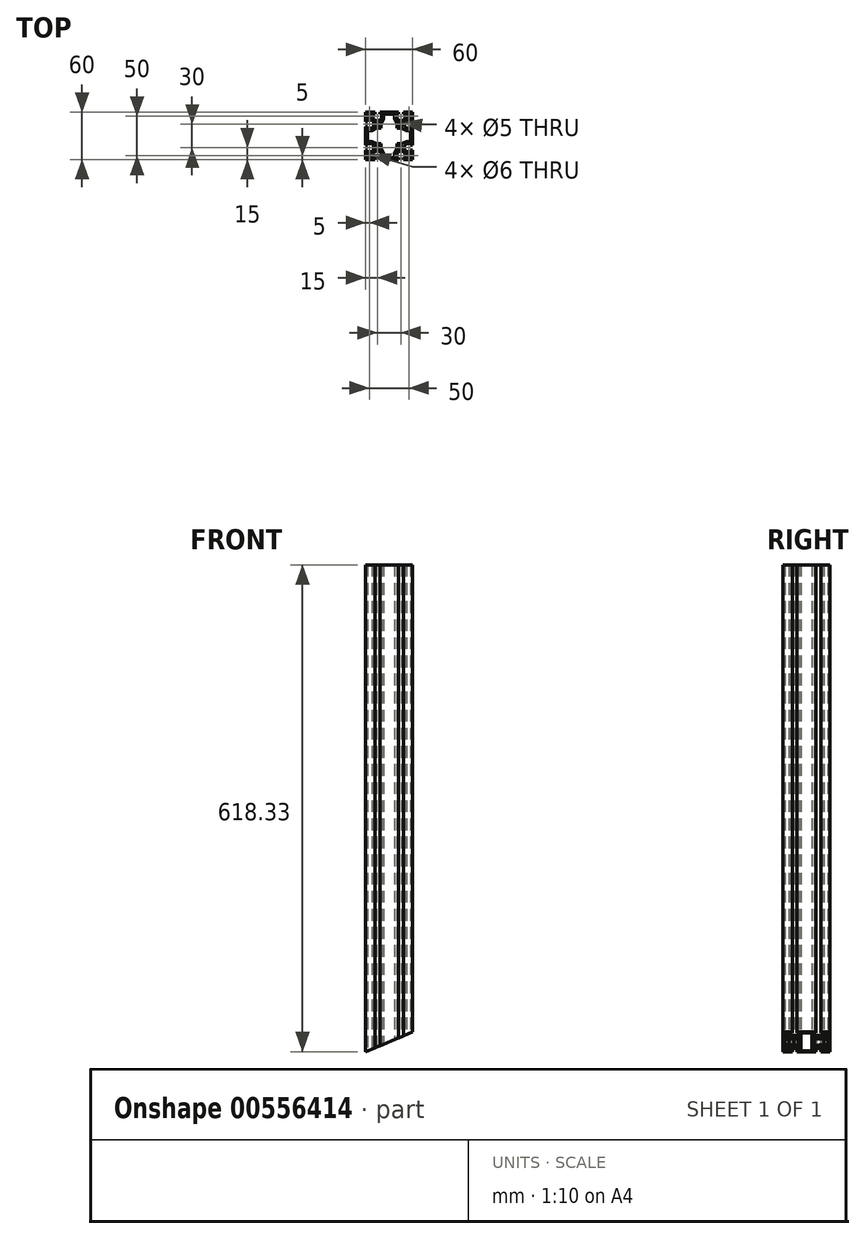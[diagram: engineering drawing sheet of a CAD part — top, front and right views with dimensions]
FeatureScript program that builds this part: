
annotation { "Feature Type Name" : "Feature", "Feature Type Description" : "" }
export const myFeature = defineFeature(function(context is Context, id is Id, definition is map)
    precondition{}
    {
        {
            var Q0;
            Q0=qCreatedBy(makeId("Top.planeOp"),FACE);
            var sketch = newSketch(context, id + "F0", { "sketchPlane" : qUnion([Q0])});
            skLineSegment(sketch, "E0.bottom", {"start": v(30, -30) * mm, "end": v(-30, -30) * mm});
            skLineSegment(sketch, "E0.top", {"start": v(30, 30) * mm, "end": v(-30, 30) * mm});
            skLineSegment(sketch, "E0.left", {"start": v(30, -30) * mm, "end": v(30, 30) * mm});
            skLineSegment(sketch, "E0.right", {"start": v(-30, -30) * mm, "end": v(-30, 30) * mm});
            skPoint(sketch, "E0.middle", {"position": v(0, 0) * mm});
            skLineSegment(sketch, "E1.top", {"start": v(-11.85, 30) * mm, "end": v(-18.15, 30) * mm});
            skLineSegment(sketch, "E1.left", {"start": v(-11.85, 27.5) * mm, "end": v(-11.85, 30) * mm});
            skLineSegment(sketch, "E1.right", {"start": v(-18.15, 27.5) * mm, "end": v(-18.15, 30) * mm});
            skPoint(sketch, "E1.middle", {"position": v(-15, 28.75) * mm});
            skLineSegment(sketch, "E2.bottom", {"start": v(-9.85, 27.5) * mm, "end": v(-11.85, 27.5) * mm});
            skLineSegment(sketch, "E2.left", {"start": v(-9.85, 27.5) * mm, "end": v(-9.85, 21.55) * mm});
            skLineSegment(sketch, "E2.right", {"start": v(-20.15, 27.5) * mm, "end": v(-20.15, 21.55) * mm});
            skPoint(sketch, "E2.middle", {"position": v(-15, 24.52) * mm});
            skArc(sketch, "E3", {"start": v(-20.15, 21.55) * mm, "mid": v(-15, 19.5) * mm, "end": v(-9.85, 21.55) * mm});
            skPoint(sketch, "E4.MirrorP", {"position": v(15, 24.52) * mm});
            skPoint(sketch, "E5.MirrorP", {"position": v(15, 28.75) * mm});
            skLineSegment(sketch, "E6.MirrorCS", {"start": v(11.85, 27.5) * mm, "end": v(11.85, 30) * mm});
            skLineSegment(sketch, "E7.MirrorCS", {"start": v(18.15, 27.5) * mm, "end": v(18.15, 30) * mm});
            skLineSegment(sketch, "E8.MirrorCS", {"start": v(9.85, 27.5) * mm, "end": v(11.85, 27.5) * mm});
            skLineSegment(sketch, "E9.MirrorCS", {"start": v(9.85, 27.5) * mm, "end": v(9.85, 21.55) * mm});
            skArc(sketch, "E10.MirrorCS", {"start": v(20.15, 21.55) * mm, "mid": v(15, 19.5) * mm, "end": v(9.85, 21.55) * mm});
            skLineSegment(sketch, "E11.MirrorCS", {"start": v(20.15, 27.5) * mm, "end": v(20.15, 21.55) * mm});
            skLineSegment(sketch, "E12.MirrorCS", {"start": v(11.85, 30) * mm, "end": v(18.15, 30) * mm});
            skLineSegment(sketch, "E13.1.0", {"start": v(27.5, 20.15) * mm, "end": v(21.55, 20.15) * mm});
            skLineSegment(sketch, "E13.1.1", {"start": v(27.5, 9.85) * mm, "end": v(21.55, 9.85) * mm});
            skArc(sketch, "E13.1.2", {"start": v(21.55, 20.15) * mm, "mid": v(19.5, 15) * mm, "end": v(21.55, 9.85) * mm});
            skLineSegment(sketch, "E13.1.3", {"start": v(27.5, -9.85) * mm, "end": v(21.55, -9.85) * mm});
            skLineSegment(sketch, "E13.1.4", {"start": v(27.5, -20.15) * mm, "end": v(21.55, -20.15) * mm});
            skPoint(sketch, "E13.1.5", {"position": v(28.75, 15) * mm});
            skPoint(sketch, "E13.1.6", {"position": v(28.75, -15) * mm});
            skArc(sketch, "E13.1.7", {"start": v(21.55, -20.15) * mm, "mid": v(19.5, -15) * mm, "end": v(21.55, -9.85) * mm});
            skPoint(sketch, "E13.1.8", {"position": v(24.52, -15) * mm});
            skPoint(sketch, "E13.1.9", {"position": v(24.52, 15) * mm});
            skLineSegment(sketch, "E13.1.10", {"start": v(27.5, 9.85) * mm, "end": v(27.5, 20.15) * mm});
            skLineSegment(sketch, "E13.1.11", {"start": v(27.5, -11.85) * mm, "end": v(27.5, -18.15) * mm});
            skLineSegment(sketch, "E13.1.12", {"start": v(30, 11.85) * mm, "end": v(30, 18.15) * mm});
            skLineSegment(sketch, "E13.1.13", {"start": v(30, -11.85) * mm, "end": v(30, -18.15) * mm});
            skLineSegment(sketch, "E13.1.14", {"start": v(27.5, 18.15) * mm, "end": v(30, 18.15) * mm});
            skLineSegment(sketch, "E13.1.15", {"start": v(27.5, 11.85) * mm, "end": v(30, 11.85) * mm});
            skLineSegment(sketch, "E13.1.16", {"start": v(27.5, 11.85) * mm, "end": v(27.5, 18.15) * mm});
            skLineSegment(sketch, "E13.1.17", {"start": v(27.5, -9.85) * mm, "end": v(27.5, -20.15) * mm});
            skLineSegment(sketch, "E13.1.18", {"start": v(27.5, -18.15) * mm, "end": v(30, -18.15) * mm});
            skLineSegment(sketch, "E13.1.19", {"start": v(27.5, -11.85) * mm, "end": v(30, -11.85) * mm});
            skLineSegment(sketch, "E13.2.0", {"start": v(20.15, -27.5) * mm, "end": v(20.15, -21.55) * mm});
            skLineSegment(sketch, "E13.2.1", {"start": v(9.85, -27.5) * mm, "end": v(9.85, -21.55) * mm});
            skArc(sketch, "E13.2.2", {"start": v(20.15, -21.55) * mm, "mid": v(15, -19.5) * mm, "end": v(9.85, -21.55) * mm});
            skLineSegment(sketch, "E13.2.3", {"start": v(-9.85, -27.5) * mm, "end": v(-9.85, -21.55) * mm});
            skLineSegment(sketch, "E13.2.4", {"start": v(-20.15, -27.5) * mm, "end": v(-20.15, -21.55) * mm});
            skPoint(sketch, "E13.2.5", {"position": v(15, -28.75) * mm});
            skPoint(sketch, "E13.2.6", {"position": v(-15, -28.75) * mm});
            skArc(sketch, "E13.2.7", {"start": v(-20.15, -21.55) * mm, "mid": v(-15, -19.5) * mm, "end": v(-9.85, -21.55) * mm});
            skPoint(sketch, "E13.2.8", {"position": v(-15, -24.52) * mm});
            skPoint(sketch, "E13.2.9", {"position": v(15, -24.52) * mm});
            skLineSegment(sketch, "E13.2.10", {"start": v(9.85, -27.5) * mm, "end": v(20.15, -27.5) * mm});
            skLineSegment(sketch, "E13.2.11", {"start": v(-11.85, -27.5) * mm, "end": v(-18.15, -27.5) * mm});
            skLineSegment(sketch, "E13.2.12", {"start": v(11.85, -30) * mm, "end": v(18.15, -30) * mm});
            skLineSegment(sketch, "E13.2.13", {"start": v(-11.85, -30) * mm, "end": v(-18.15, -30) * mm});
            skLineSegment(sketch, "E13.2.14", {"start": v(18.15, -27.5) * mm, "end": v(18.15, -30) * mm});
            skLineSegment(sketch, "E13.2.15", {"start": v(11.85, -27.5) * mm, "end": v(11.85, -30) * mm});
            skLineSegment(sketch, "E13.2.16", {"start": v(11.85, -27.5) * mm, "end": v(18.15, -27.5) * mm});
            skLineSegment(sketch, "E13.2.17", {"start": v(-9.85, -27.5) * mm, "end": v(-20.15, -27.5) * mm});
            skLineSegment(sketch, "E13.2.18", {"start": v(-18.15, -27.5) * mm, "end": v(-18.15, -30) * mm});
            skLineSegment(sketch, "E13.2.19", {"start": v(-11.85, -27.5) * mm, "end": v(-11.85, -30) * mm});
            skLineSegment(sketch, "E13.3.0", {"start": v(-27.5, -20.15) * mm, "end": v(-21.55, -20.15) * mm});
            skLineSegment(sketch, "E13.3.1", {"start": v(-27.5, -9.85) * mm, "end": v(-21.55, -9.85) * mm});
            skArc(sketch, "E13.3.2", {"start": v(-21.55, -20.15) * mm, "mid": v(-19.5, -15) * mm, "end": v(-21.55, -9.85) * mm});
            skLineSegment(sketch, "E13.3.3", {"start": v(-27.5, 9.85) * mm, "end": v(-21.55, 9.85) * mm});
            skLineSegment(sketch, "E13.3.4", {"start": v(-27.5, 20.15) * mm, "end": v(-21.55, 20.15) * mm});
            skPoint(sketch, "E13.3.5", {"position": v(-28.75, -15) * mm});
            skPoint(sketch, "E13.3.6", {"position": v(-28.75, 15) * mm});
            skArc(sketch, "E13.3.7", {"start": v(-21.55, 20.15) * mm, "mid": v(-19.5, 15) * mm, "end": v(-21.55, 9.85) * mm});
            skPoint(sketch, "E13.3.8", {"position": v(-24.52, 15) * mm});
            skPoint(sketch, "E13.3.9", {"position": v(-24.52, -15) * mm});
            skLineSegment(sketch, "E13.3.10", {"start": v(-27.5, -9.85) * mm, "end": v(-27.5, -20.15) * mm});
            skLineSegment(sketch, "E13.3.11", {"start": v(-27.5, 11.85) * mm, "end": v(-27.5, 18.15) * mm});
            skLineSegment(sketch, "E13.3.12", {"start": v(-30, -11.85) * mm, "end": v(-30, -18.15) * mm});
            skLineSegment(sketch, "E13.3.13", {"start": v(-30, 11.85) * mm, "end": v(-30, 18.15) * mm});
            skLineSegment(sketch, "E13.3.14", {"start": v(-27.5, -18.15) * mm, "end": v(-30, -18.15) * mm});
            skLineSegment(sketch, "E13.3.15", {"start": v(-27.5, -11.85) * mm, "end": v(-30, -11.85) * mm});
            skLineSegment(sketch, "E13.3.16", {"start": v(-27.5, -11.85) * mm, "end": v(-27.5, -18.15) * mm});
            skLineSegment(sketch, "E13.3.17", {"start": v(-27.5, 9.85) * mm, "end": v(-27.5, 20.15) * mm});
            skLineSegment(sketch, "E13.3.18", {"start": v(-27.5, 18.15) * mm, "end": v(-30, 18.15) * mm});
            skLineSegment(sketch, "E13.3.19", {"start": v(-27.5, 11.85) * mm, "end": v(-30, 11.85) * mm});
            skLineSegment(sketch, "E13.anchor1", {"start": v(0, 0) * mm, "end": v(-20.15, 21.55) * mm, "construction": true});
            skLineSegment(sketch, "E13.anchor2", {"start": v(0, 0) * mm, "end": v(-21.55, -20.15) * mm, "construction": true});
            skLineSegment(sketch, "E14.trimOffspring", {"start": v(-18.15, 27.5) * mm, "end": v(-20.15, 27.5) * mm});
            skLineSegment(sketch, "E15.trimOffspring", {"start": v(18.15, 27.5) * mm, "end": v(20.15, 27.5) * mm});
            skCircle(sketch, "E16", {"center": v(-15, 15) * mm, "radius": 2.5 * mm});
            skCircle(sketch, "E17", {"center": v(-25, 25) * mm, "radius": 3 * mm});
            skCircle(sketch, "E18.MirrorC", {"center": v(25, 25) * mm, "radius": 3 * mm});
            skCircle(sketch, "E19.MirrorC", {"center": v(25, -25) * mm, "radius": 3 * mm});
            skCircle(sketch, "E20.MirrorC", {"center": v(-25, -25) * mm, "radius": 3 * mm});
            skCircle(sketch, "E21.MirrorC", {"center": v(15, 15) * mm, "radius": 2.5 * mm});
            skCircle(sketch, "E22.MirrorC", {"center": v(15, -15) * mm, "radius": 2.5 * mm});
            skCircle(sketch, "E23.MirrorC", {"center": v(-15, -15) * mm, "radius": 2.5 * mm});
            skLineSegment(sketch, "E24", {"start": v(-7, 27.5) * mm, "end": v(0, 27.5) * mm});
            skLineSegment(sketch, "E25", {"start": v(-7, 27.5) * mm, "end": v(-7, 22) * mm});
            skLineSegment(sketch, "E26", {"start": v(-10, 10) * mm, "end": v(-10, 16) * mm});
            skLineSegment(sketch, "E27", {"start": v(-10, 16) * mm, "end": v(-7, 22) * mm});
            skLineSegment(sketch, "E28.MirrorCS", {"start": v(10, 10) * mm, "end": v(10, 16) * mm});
            skLineSegment(sketch, "E29.MirrorCS", {"start": v(10, 16) * mm, "end": v(7, 22) * mm});
            skLineSegment(sketch, "E30.MirrorCS", {"start": v(7, 27.5) * mm, "end": v(0, 27.5) * mm});
            skLineSegment(sketch, "E31.MirrorCS", {"start": v(7, 27.5) * mm, "end": v(7, 22) * mm});
            skLineSegment(sketch, "E32.1.0", {"start": v(-10, -10) * mm, "end": v(-16, -10) * mm});
            skLineSegment(sketch, "E32.1.1", {"start": v(-16, -10) * mm, "end": v(-22, -7) * mm});
            skLineSegment(sketch, "E32.1.2", {"start": v(-27.5, -7) * mm, "end": v(-22, -7) * mm});
            skLineSegment(sketch, "E32.1.3", {"start": v(-27.5, -7) * mm, "end": v(-27.5, 0) * mm});
            skLineSegment(sketch, "E32.1.4", {"start": v(-27.5, 7) * mm, "end": v(-27.5, 0) * mm});
            skLineSegment(sketch, "E32.1.5", {"start": v(-27.5, 7) * mm, "end": v(-22, 7) * mm});
            skLineSegment(sketch, "E32.1.6", {"start": v(-16, 10) * mm, "end": v(-22, 7) * mm});
            skLineSegment(sketch, "E32.1.7", {"start": v(-10, 10) * mm, "end": v(-16, 10) * mm});
            skLineSegment(sketch, "E32.2.0", {"start": v(10, -10) * mm, "end": v(10, -16) * mm});
            skLineSegment(sketch, "E32.2.1", {"start": v(10, -16) * mm, "end": v(7, -22) * mm});
            skLineSegment(sketch, "E32.2.2", {"start": v(7, -27.5) * mm, "end": v(7, -22) * mm});
            skLineSegment(sketch, "E32.2.3", {"start": v(7, -27.5) * mm, "end": v(0, -27.5) * mm});
            skLineSegment(sketch, "E32.2.4", {"start": v(-7, -27.5) * mm, "end": v(0, -27.5) * mm});
            skLineSegment(sketch, "E32.2.5", {"start": v(-7, -27.5) * mm, "end": v(-7, -22) * mm});
            skLineSegment(sketch, "E32.2.6", {"start": v(-10, -16) * mm, "end": v(-7, -22) * mm});
            skLineSegment(sketch, "E32.2.7", {"start": v(-10, -10) * mm, "end": v(-10, -16) * mm});
            skLineSegment(sketch, "E32.3.0", {"start": v(10, 10) * mm, "end": v(16, 10) * mm});
            skLineSegment(sketch, "E32.3.1", {"start": v(16, 10) * mm, "end": v(22, 7) * mm});
            skLineSegment(sketch, "E32.3.2", {"start": v(27.5, 7) * mm, "end": v(22, 7) * mm});
            skLineSegment(sketch, "E32.3.3", {"start": v(27.5, 7) * mm, "end": v(27.5, 0) * mm});
            skLineSegment(sketch, "E32.3.4", {"start": v(27.5, -7) * mm, "end": v(27.5, 0) * mm});
            skLineSegment(sketch, "E32.3.5", {"start": v(27.5, -7) * mm, "end": v(22, -7) * mm});
            skLineSegment(sketch, "E32.3.6", {"start": v(16, -10) * mm, "end": v(22, -7) * mm});
            skLineSegment(sketch, "E32.3.7", {"start": v(10, -10) * mm, "end": v(16, -10) * mm});
            skSolve(sketch);
        }
        {
            var Q0;
            {var subQ30=sQuery(id+"F0.wireOp",EDGE,"E1.left");Q0=makeQuery(id+"F0.imprint","IMPRINT",FACE,{"disambiguationData":[TD([[makeQuery(id+"F0.imprint","IMPRINT",EDGE,{"derivedFrom":subQ30}),-1.0]])]});}
            extrude(context, id + "F1", {"entities" : qUnion([Q0]), "depth" : 618.33 * mm, "offsetDistance" : 25 * mm});
        }
        {
            var Q0;
            Q0=makeQuery(id+"F1.opExtrude","SWEPT_EDGE",EDGE,{"disambiguationData":[OSD([sQuery(id+"F0.wireOp",EDGE,"E24"),sQuery(id+"F0.wireOp",EDGE,"E25")])]});
            var Q1;
            Q1=makeQuery(id+"F1.opExtrude","SWEPT_EDGE",EDGE,{"disambiguationData":[OSD([sQuery(id+"F0.wireOp",EDGE,"E30.MirrorCS"),sQuery(id+"F0.wireOp",EDGE,"E31.MirrorCS")])]});
            var Q2;
            Q2=makeQuery(id+"F1.opExtrude","SWEPT_EDGE",EDGE,{"disambiguationData":[OSD([sQuery(id+"F0.wireOp",EDGE,"840db5bc-c403-45cd-90c7-254e62d9e8c5.3.2"),sQuery(id+"F0.wireOp",EDGE,"840db5bc-c403-45cd-90c7-254e62d9e8c5.3.3")])]});
            var Q3;
            Q3=makeQuery(id+"F1.opExtrude","SWEPT_EDGE",EDGE,{"disambiguationData":[OSD([sQuery(id+"F0.wireOp",EDGE,"840db5bc-c403-45cd-90c7-254e62d9e8c5.3.4"),sQuery(id+"F0.wireOp",EDGE,"840db5bc-c403-45cd-90c7-254e62d9e8c5.3.5")])]});
            var Q4;
            Q4=makeQuery(id+"F1.opExtrude","SWEPT_EDGE",EDGE,{"disambiguationData":[OSD([sQuery(id+"F0.wireOp",EDGE,"840db5bc-c403-45cd-90c7-254e62d9e8c5.1.4"),sQuery(id+"F0.wireOp",EDGE,"840db5bc-c403-45cd-90c7-254e62d9e8c5.1.5")])]});
            var Q5;
            Q5=makeQuery(id+"F1.opExtrude","SWEPT_EDGE",EDGE,{"disambiguationData":[OSD([sQuery(id+"F0.wireOp",EDGE,"840db5bc-c403-45cd-90c7-254e62d9e8c5.1.2"),sQuery(id+"F0.wireOp",EDGE,"840db5bc-c403-45cd-90c7-254e62d9e8c5.1.3")])]});
            var Q6;
            Q6=makeQuery(id+"F1.opExtrude","SWEPT_EDGE",EDGE,{"disambiguationData":[OSD([sQuery(id+"F0.wireOp",EDGE,"840db5bc-c403-45cd-90c7-254e62d9e8c5.2.2"),sQuery(id+"F0.wireOp",EDGE,"840db5bc-c403-45cd-90c7-254e62d9e8c5.2.3")])]});
            var Q7;
            Q7=makeQuery(id+"F1.opExtrude","SWEPT_EDGE",EDGE,{"disambiguationData":[OSD([sQuery(id+"F0.wireOp",EDGE,"840db5bc-c403-45cd-90c7-254e62d9e8c5.2.4"),sQuery(id+"F0.wireOp",EDGE,"840db5bc-c403-45cd-90c7-254e62d9e8c5.2.5")])]});
            fillet(context, id + "F2", {"entities" : qUnion([Q0, Q1, Q2, Q3, Q4, Q5, Q6, Q7]), "radius" : 2 * mm, "tangentPropagation" : true, "allowEdgeOverflow" : false});
        }
        {
            var Q0;
            Q0=makeQuery(id+"F1.opExtrude","SWEPT_EDGE",EDGE,{"disambiguationData":[OSD([sQuery(id+"F0.wireOp",EDGE,"E26"),sQuery(id+"F0.wireOp",EDGE,"E27")])]});
            var Q1;
            Q1=makeQuery(id+"F1.opExtrude","SWEPT_EDGE",EDGE,{"disambiguationData":[OSD([sQuery(id+"F0.wireOp",EDGE,"E28.MirrorCS"),sQuery(id+"F0.wireOp",EDGE,"E29.MirrorCS")])]});
            var Q2;
            Q2=makeQuery(id+"F1.opExtrude","SWEPT_EDGE",EDGE,{"disambiguationData":[OSD([sQuery(id+"F0.wireOp",EDGE,"840db5bc-c403-45cd-90c7-254e62d9e8c5.3.0"),sQuery(id+"F0.wireOp",EDGE,"840db5bc-c403-45cd-90c7-254e62d9e8c5.3.1")])]});
            var Q3;
            Q3=makeQuery(id+"F1.opExtrude","SWEPT_EDGE",EDGE,{"disambiguationData":[OSD([sQuery(id+"F0.wireOp",EDGE,"840db5bc-c403-45cd-90c7-254e62d9e8c5.1.6"),sQuery(id+"F0.wireOp",EDGE,"840db5bc-c403-45cd-90c7-254e62d9e8c5.1.7")])]});
            var Q4;
            Q4=makeQuery(id+"F1.opExtrude","SWEPT_EDGE",EDGE,{"disambiguationData":[OSD([sQuery(id+"F0.wireOp",EDGE,"840db5bc-c403-45cd-90c7-254e62d9e8c5.1.0"),sQuery(id+"F0.wireOp",EDGE,"840db5bc-c403-45cd-90c7-254e62d9e8c5.1.1")])]});
            var Q5;
            Q5=makeQuery(id+"F1.opExtrude","SWEPT_EDGE",EDGE,{"disambiguationData":[OSD([sQuery(id+"F0.wireOp",EDGE,"840db5bc-c403-45cd-90c7-254e62d9e8c5.3.6"),sQuery(id+"F0.wireOp",EDGE,"840db5bc-c403-45cd-90c7-254e62d9e8c5.3.7")])]});
            var Q6;
            Q6=makeQuery(id+"F1.opExtrude","SWEPT_EDGE",EDGE,{"disambiguationData":[OSD([sQuery(id+"F0.wireOp",EDGE,"840db5bc-c403-45cd-90c7-254e62d9e8c5.2.0"),sQuery(id+"F0.wireOp",EDGE,"840db5bc-c403-45cd-90c7-254e62d9e8c5.2.1")])]});
            var Q7;
            Q7=makeQuery(id+"F1.opExtrude","SWEPT_EDGE",EDGE,{"disambiguationData":[OSD([sQuery(id+"F0.wireOp",EDGE,"840db5bc-c403-45cd-90c7-254e62d9e8c5.2.6"),sQuery(id+"F0.wireOp",EDGE,"840db5bc-c403-45cd-90c7-254e62d9e8c5.2.7")])]});
            fillet(context, id + "F3", {"entities" : qUnion([Q0, Q1, Q2, Q3, Q4, Q5, Q6, Q7]), "radius" : 7 * mm, "tangentPropagation" : true, "allowEdgeOverflow" : false});
        }
        {
            var Q0;
            Q0=qCreatedBy(makeId("Front.planeOp"),FACE);
            var sketch = newSketch(context, id + "F4", { "sketchPlane" : qUnion([Q0])});
            skLineSegment(sketch, "E33.bottom", {"start": v(-30, 0) * mm, "end": v(227.68, 106.74) * mm});
            skLineSegment(sketch, "E33.top", {"start": v(35.18, -157.35) * mm, "end": v(292.86, -50.61) * mm});
            skLineSegment(sketch, "E33.left", {"start": v(-30, 0) * mm, "end": v(35.18, -157.35) * mm});
            skLineSegment(sketch, "E33.right", {"start": v(227.68, 106.74) * mm, "end": v(292.86, -50.61) * mm});
            skSolve(sketch);
        }
        {
            var Q0;
            Q0=qSketchRegion(id+"F4",true);
            extrude(context, id + "F5", {"entities" : qUnion([Q0]), "operationType" : NewBodyOperationType.REMOVE, "depth" : 30 * mm, "offsetDistance" : 25 * mm, "hasSecondDirection" : true, "secondDirectionOppositeDirection" : true, "secondDirectionDepth" : 30 * mm});
        }
    });
